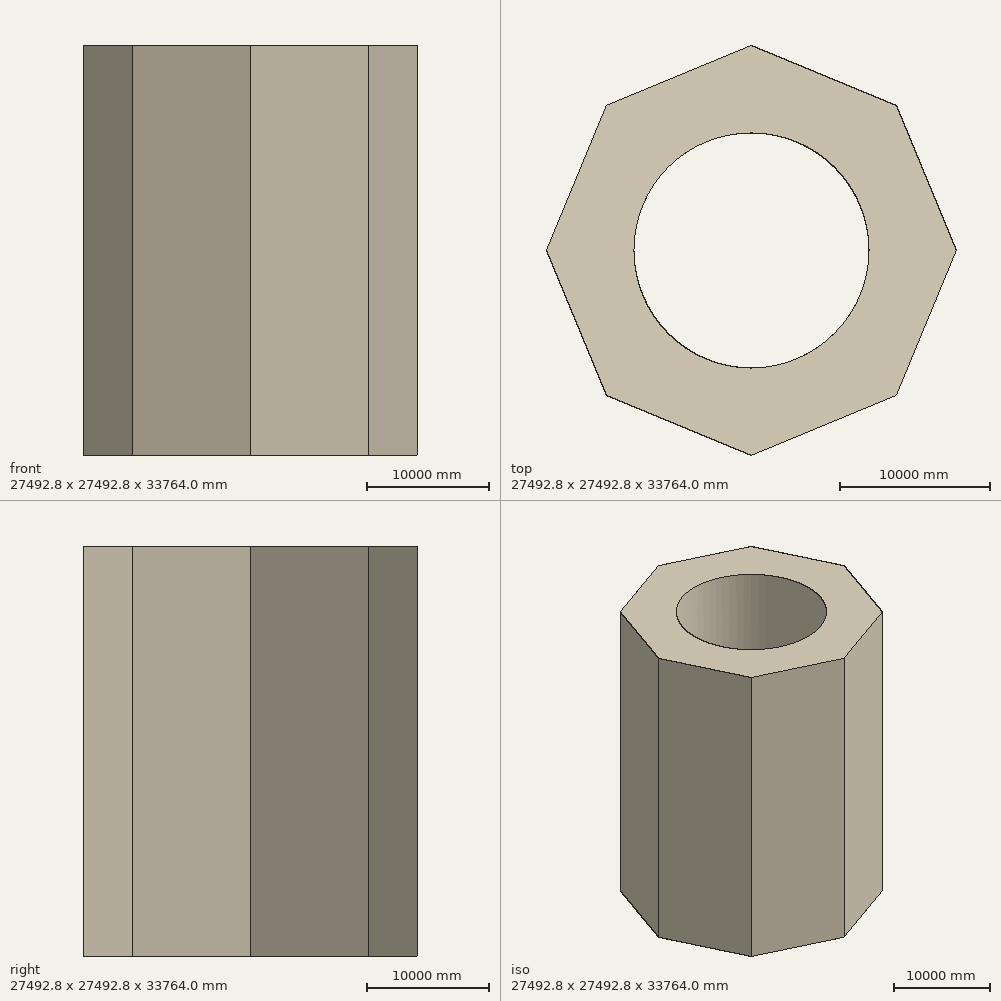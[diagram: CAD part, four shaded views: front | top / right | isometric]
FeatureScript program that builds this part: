
annotation { "Feature Type Name" : "Feature", "Feature Type Description" : "" }
export const myFeature = defineFeature(function(context is Context, id is Id, definition is map)
    precondition{}
    {
        {
            var Q0;
            Q0=qCreatedBy(makeId("Top.planeOp"),FACE);
            var sketch = newSketch(context, id + "F0", { "sketchPlane" : qUnion([Q0])});
            skCircle(sketch, "E0.cCircle", {"center": v(0, 0) * mm, "radius": 12700 * mm, "construction": true});
            skLineSegment(sketch, "E0.0", {"start": v(0, 13746.38) * mm, "end": v(9720.16, 9720.16) * mm});
            skLineSegment(sketch, "E0.1", {"start": v(9720.16, 9720.16) * mm, "end": v(13746.38, 0) * mm});
            skLineSegment(sketch, "E0.2", {"start": v(13746.38, 0) * mm, "end": v(9720.16, -9720.16) * mm});
            skLineSegment(sketch, "E0.3", {"start": v(9720.16, -9720.16) * mm, "end": v(0, -13746.38) * mm});
            skLineSegment(sketch, "E0.4", {"start": v(0, -13746.38) * mm, "end": v(-9720.16, -9720.16) * mm});
            skLineSegment(sketch, "E0.5", {"start": v(-9720.16, -9720.16) * mm, "end": v(-13746.38, 0) * mm});
            skLineSegment(sketch, "E0.6", {"start": v(-13746.38, 0) * mm, "end": v(-9720.16, 9720.16) * mm});
            skLineSegment(sketch, "E0.7", {"start": v(-9720.16, 9720.16) * mm, "end": v(0, 13746.38) * mm});
            skPoint(sketch, "E0.0.midPoint", {"position": v(4860.08, 11733.27) * mm});
            skSolve(sketch);
        }
        {
            var Q0;
            Q0=makeQuery(id+"F0.imprint","IMPRINT",FACE,{"disambiguationData":[TD([[makeQuery(id+"F0.imprint","IMPRINT",EDGE,{"derivedFrom":sQuery(id+"F0.wireOp",EDGE,"E0.0")}),-1.0]])]});
            extrude(context, id + "F1", {"entities" : qUnion([Q0]), "depth" : 13472.33 * mm, "hasSecondDirection" : true, "secondDirectionOppositeDirection" : true, "secondDirectionDepth" : 20291.69 * mm});
        }
        {
            var Q0;
            Q0=makeQuery(id+"F1.opExtrude","CAP_FACE",FACE,{"disambiguationData":[OSD([sQuery(id+"F0.wireOp",EDGE,"E0.0"),sQuery(id+"F0.wireOp",EDGE,"E0.1"),sQuery(id+"F0.wireOp",EDGE,"E0.2"),sQuery(id+"F0.wireOp",EDGE,"E0.3"),sQuery(id+"F0.wireOp",EDGE,"E0.4"),sQuery(id+"F0.wireOp",EDGE,"E0.5"),sQuery(id+"F0.wireOp",EDGE,"E0.6"),sQuery(id+"F0.wireOp",EDGE,"E0.7")])],"isStart":true});
            var sketch = newSketch(context, id + "F2", { "sketchPlane" : qUnion([Q0])});
            skCircle(sketch, "E1", {"center": v(0, 0) * mm, "radius": 7882.37 * mm});
            skSolve(sketch);
        }
        {
            var Q0;
            Q0 = qSketchRegion(id + "F2", true);
            extrude(context, id + "F3", {"entities" : qUnion([Q0]), "operationType" : NewBodyOperationType.REMOVE, "endBound" : BoundingType.THROUGH_ALL, "oppositeDirection" : true, "depth" : 25.4 * mm});
        }
    });
